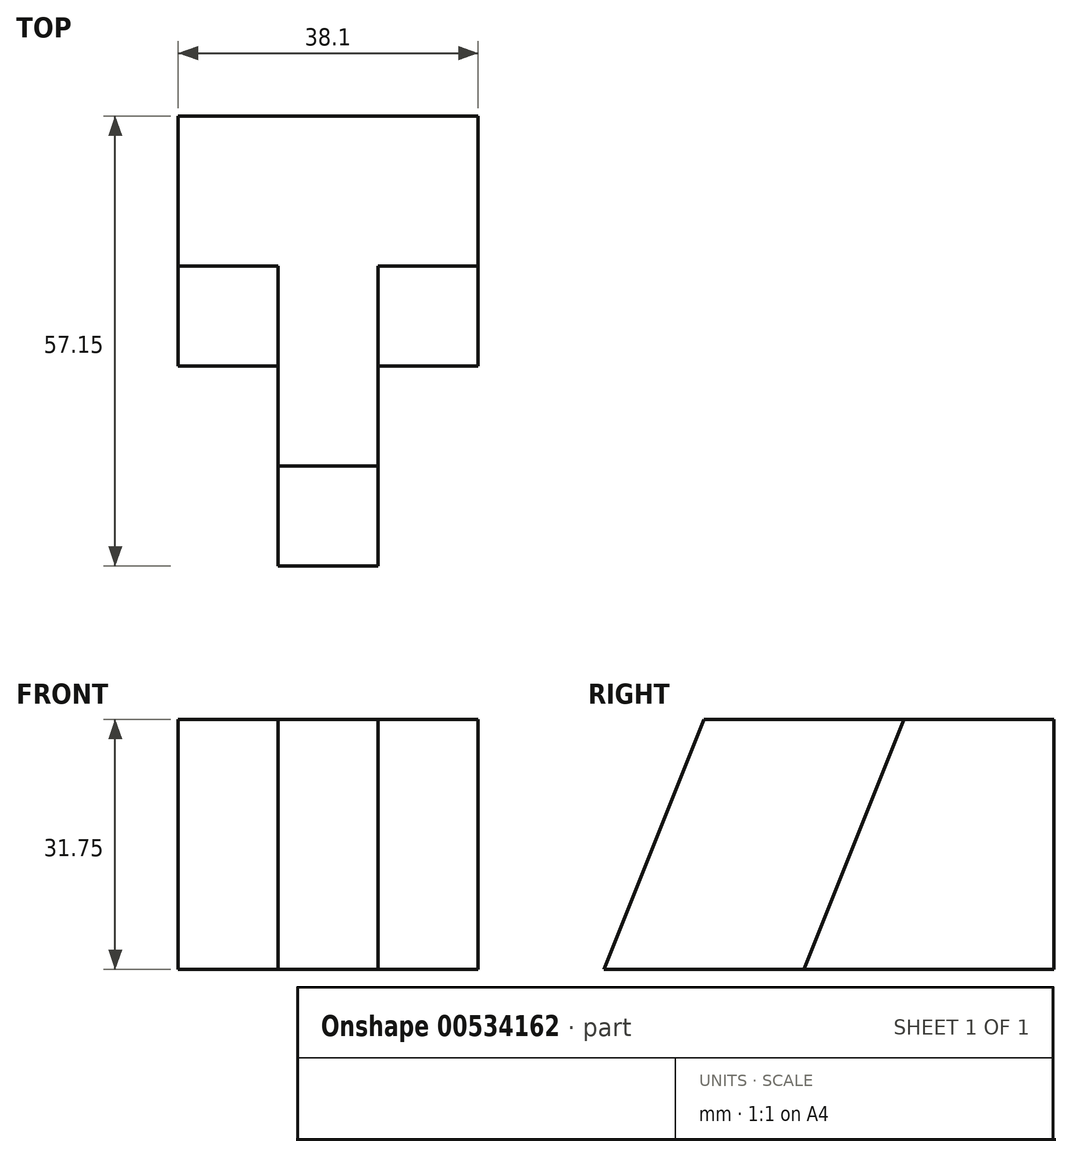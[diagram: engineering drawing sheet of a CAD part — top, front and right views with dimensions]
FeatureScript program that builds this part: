
annotation { "Feature Type Name" : "Feature", "Feature Type Description" : "" }
export const myFeature = defineFeature(function(context is Context, id is Id, definition is map)
    precondition{}
    {
        {
            var Q0;
            Q0=qCreatedBy(makeId("Right.planeOp"),FACE);
            var sketch = newSketch(context, id + "F0", { "sketchPlane" : qUnion([Q0])});
            skLineSegment(sketch, "E0", {"start": v(0, 31.75) * mm, "end": v(0, 0) * mm});
            skLineSegment(sketch, "E1", {"start": v(0, 0) * mm, "end": v(-57.15, 0) * mm});
            skLineSegment(sketch, "E2", {"start": v(0, 31.75) * mm, "end": v(-44.45, 31.75) * mm});
            skLineSegment(sketch, "E3", {"start": v(-44.45, 31.75) * mm, "end": v(-57.15, 0) * mm});
            skSolve(sketch);
        }
        {
            var Q0;
            Q0=makeQuery(id+"F0.imprint","IMPRINT",FACE,{"disambiguationData":[TD([[makeQuery(id+"F0.imprint","IMPRINT",EDGE,{"derivedFrom":sQuery(id+"F0.wireOp",EDGE,"E0")}),-1.0]])]});
            extrude(context, id + "F1", {"entities" : qUnion([Q0]), "depth" : 38.1 * mm, "offsetDistance" : 25.4 * mm});
        }
        {
            var Q0;
            Q0=makeQuery(id+"F1.opExtrude","CAP_FACE",FACE,{"disambiguationData":[OSD([sQuery(id+"F0.wireOp",EDGE,"E0"),sQuery(id+"F0.wireOp",EDGE,"E1"),sQuery(id+"F0.wireOp",EDGE,"E2"),sQuery(id+"F0.wireOp",EDGE,"E3")])],"isStart":true});
            var sketch = newSketch(context, id + "F2", { "sketchPlane" : qUnion([Q0])});
            skLineSegment(sketch, "E4", {"start": v(19.05, 31.75) * mm, "end": v(31.75, 0) * mm});
            skSolve(sketch);
        }
        {
            var Q0;
            {var subQ0=sQuery(id+"F2.wireOp",EDGE,"E4");Q0=makeQuery(id+"F2.imprint","IMPRINT",FACE,{"disambiguationData":[TD([[makeQuery(id+"F2.imprint","IMPRINT",EDGE,{"derivedFrom":subQ0}),1.0]])]});}
            extrude(context, id + "F3", {"entities" : qUnion([Q0]), "operationType" : NewBodyOperationType.REMOVE, "oppositeDirection" : true, "depth" : 12.7 * mm, "offsetDistance" : 25.4 * mm});
        }
        {
            var Q0;
            Q0=makeQuery(id+"F1.opExtrude","CAP_FACE",FACE,{"disambiguationData":[OSD([sQuery(id+"F0.wireOp",EDGE,"E0"),sQuery(id+"F0.wireOp",EDGE,"E1"),sQuery(id+"F0.wireOp",EDGE,"E2"),sQuery(id+"F0.wireOp",EDGE,"E3")])],"isStart":false});
            var sketch = newSketch(context, id + "F4", { "sketchPlane" : qUnion([Q0])});
            skLineSegment(sketch, "E5", {"start": v(-19.05, 31.75) * mm, "end": v(-31.75, 0) * mm});
            skSolve(sketch);
        }
        {
            var Q0;
            {var subQ0=sQuery(id+"F4.wireOp",EDGE,"E5");Q0=makeQuery(id+"F4.imprint","IMPRINT",FACE,{"disambiguationData":[TD([[makeQuery(id+"F4.imprint","IMPRINT",EDGE,{"derivedFrom":subQ0}),-1.0]])]});}
            extrude(context, id + "F5", {"entities" : qUnion([Q0]), "operationType" : NewBodyOperationType.REMOVE, "oppositeDirection" : true, "depth" : 12.7 * mm, "offsetDistance" : 25.4 * mm});
        }
    });
